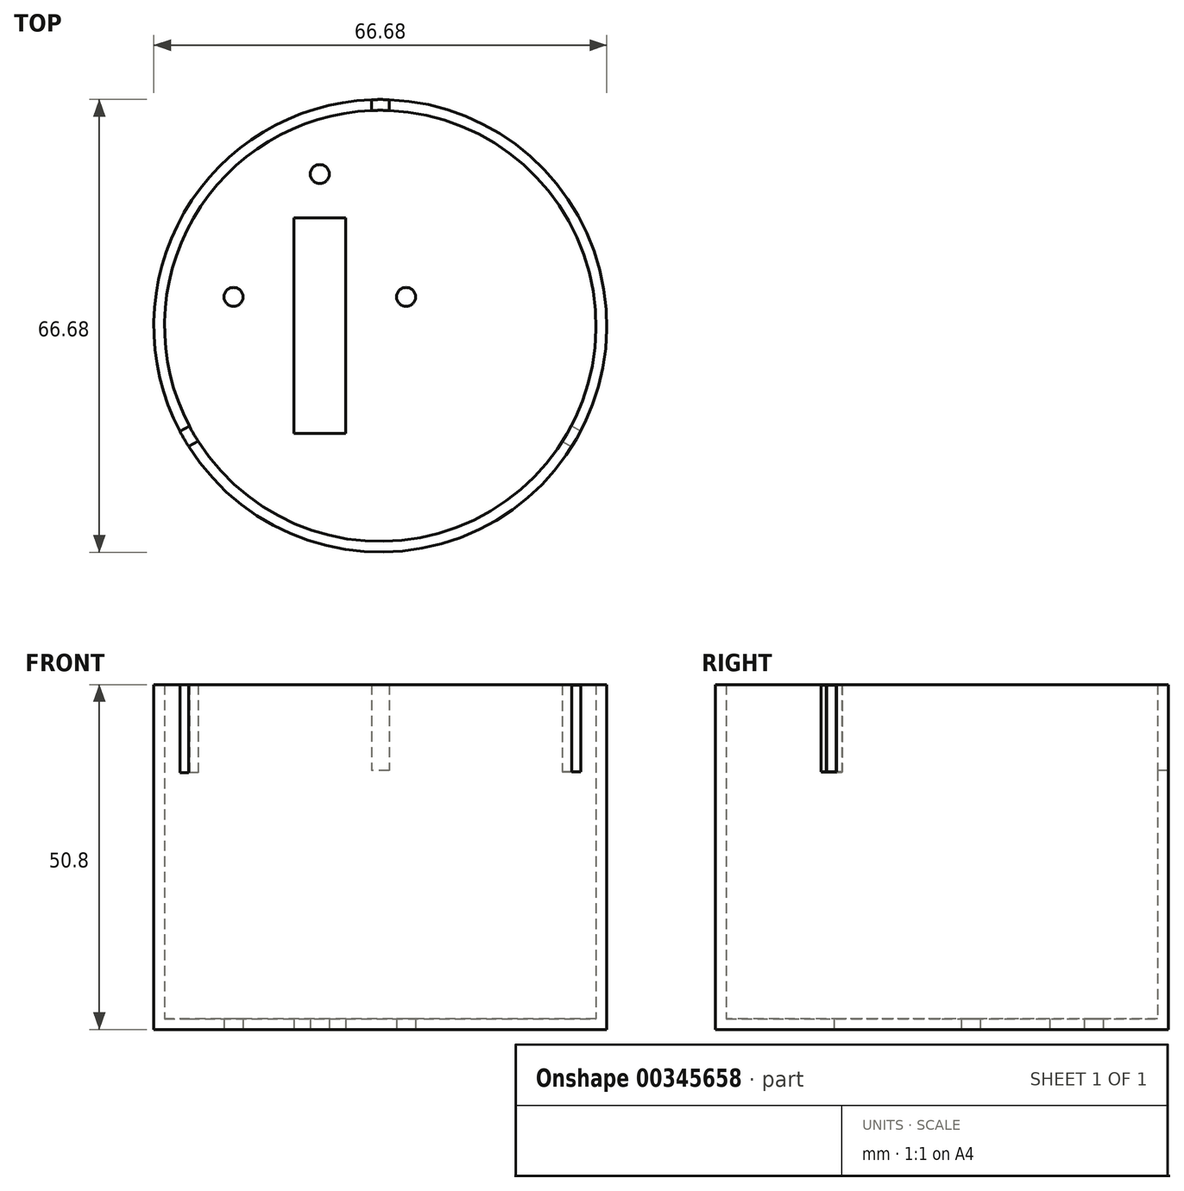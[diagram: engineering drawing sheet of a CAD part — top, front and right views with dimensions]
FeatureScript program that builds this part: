
annotation { "Feature Type Name" : "Feature", "Feature Type Description" : "" }
export const myFeature = defineFeature(function(context is Context, id is Id, definition is map)
    precondition{}
    {
        {
            var Q0;
            Q0=qCreatedBy(makeId("Top.planeOp"),FACE);
            var sketch = newSketch(context, id + "F0", { "sketchPlane" : qUnion([Q0])});
            skCircle(sketch, "E0", {"center": v(0, 0) * mm, "radius": 33.34 * mm});
            skSolve(sketch);
        }
        {
            var Q0;
            Q0=makeQuery(id+"F0.imprint","IMPRINT",FACE,{"disambiguationData":[TD([[makeQuery(id+"F0.imprint","IMPRINT",EDGE,{"derivedFrom":sQuery(id+"F0.wireOp",EDGE,"E0")}),1.0]])]});
            extrude(context, id + "F1", {"entities" : qUnion([Q0]), "depth" : 50.8 * mm});
        }
        {
            var Q0;
            Q0=makeQuery(id+"F1.opExtrude","CAP_FACE",FACE,{"disambiguationData":[OSD([sQuery(id+"F0.wireOp",EDGE,"E0")])],"isStart":false});
            shell(context, id + "F2", {"entities" : qUnion([Q0]), "thickness" : 1.59 * mm});
        }
        {
            var Q0;
            Q0=qCreatedBy(makeId("Top.planeOp"),FACE);
            var sketch = newSketch(context, id + "F3", { "sketchPlane" : qUnion([Q0])});
            skLineSegment(sketch, "E1", {"start": v(58.26, 0) * mm, "end": v(0, 0) * mm, "construction": true});
            skLineSegment(sketch, "E2", {"start": v(0, 0) * mm, "end": v(47.3, -27.3) * mm, "construction": true});
            skLineSegment(sketch, "E3", {"start": v(-50.45, 0) * mm, "end": v(0, 0) * mm, "construction": true});
            skLineSegment(sketch, "E4", {"start": v(0, 0) * mm, "end": v(-51.5, -29.73) * mm, "construction": true});
            skSolve(sketch);
        }
        {
            var Q0;
            Q0=sQuery(id+"F3.wireOp",EDGE,"E4");
            var Q1;
            Q1=sQuery(id+"F3.wireOp",VERTEX,"E4.start");
            cPlane(context, id + "F4", {"entities" : qUnion([Q0, Q1]), "cplaneType" : CPlaneType.LINE_POINT, "offset" : 25.4 * mm, "width" : 152.4 * mm, "height" : 152.4 * mm});
        }
        {
            var Q0;
            Q0=qCreatedBy(id+"F4.planeOp",FACE);
            cPlane(context, id + "F5", {"entities" : qUnion([Q0]), "cplaneType" : CPlaneType.OFFSET, "offset" : 33.34 * mm, "width" : 152.4 * mm, "height" : 152.4 * mm});
        }
        {
            var Q0;
            Q0=qCreatedBy(id+"F5.planeOp",FACE);
            var sketch = newSketch(context, id + "F6", { "sketchPlane" : qUnion([Q0])});
            skLineSegment(sketch, "E5.bottom", {"start": v(-1.27, 37.8) * mm, "end": v(1.27, 37.8) * mm});
            skLineSegment(sketch, "E5.top", {"start": v(-1.27, 51) * mm, "end": v(1.27, 51) * mm});
            skLineSegment(sketch, "E5.left", {"start": v(-1.27, 37.8) * mm, "end": v(-1.27, 51) * mm});
            skLineSegment(sketch, "E5.right", {"start": v(1.27, 37.8) * mm, "end": v(1.27, 51) * mm});
            skPoint(sketch, "E5.middle", {"position": v(0, 44.4) * mm});
            skSolve(sketch);
        }
        {
            var Q0;
            Q0=makeQuery(id+"F6.imprint","IMPRINT",FACE,{"disambiguationData":[TD([[makeQuery(id+"F6.imprint","IMPRINT",EDGE,{"derivedFrom":sQuery(id+"F6.wireOp",EDGE,"E5.bottom")}),1.0]])]});
            extrude(context, id + "F7", {"entities" : qUnion([Q0]), "operationType" : NewBodyOperationType.REMOVE, "oppositeDirection" : true, "depth" : 12.7 * mm});
        }
        {
            var Q0;
            Q0=sQuery(id+"F3.wireOp",EDGE,"E2");
            var Q1;
            Q1=sQuery(id+"F3.wireOp",VERTEX,"E4.start");
            cPlane(context, id + "F8", {"entities" : qUnion([Q0, Q1]), "cplaneType" : CPlaneType.LINE_POINT, "offset" : 25.4 * mm, "width" : 152.4 * mm, "height" : 152.4 * mm});
        }
        {
            var Q0;
            Q0=qCreatedBy(id+"F8.planeOp",FACE);
            cPlane(context, id + "F9", {"entities" : qUnion([Q0]), "cplaneType" : CPlaneType.OFFSET, "offset" : 33.27 * mm, "width" : 152.4 * mm, "height" : 152.4 * mm});
        }
        {
            var Q0;
            Q0=qCreatedBy(id+"F9.planeOp",FACE);
            var sketch = newSketch(context, id + "F10", { "sketchPlane" : qUnion([Q0])});
            skLineSegment(sketch, "E6.bottom", {"start": v(-1.34, 37.95) * mm, "end": v(1.34, 37.95) * mm});
            skLineSegment(sketch, "E6.top", {"start": v(-1.34, 50.73) * mm, "end": v(1.34, 50.73) * mm});
            skLineSegment(sketch, "E6.left", {"start": v(-1.34, 37.95) * mm, "end": v(-1.34, 50.73) * mm});
            skLineSegment(sketch, "E6.right", {"start": v(1.34, 37.95) * mm, "end": v(1.34, 50.73) * mm});
            skPoint(sketch, "E6.middle", {"position": v(0, 44.34) * mm});
            skSolve(sketch);
        }
        {
            var Q0;
            Q0=makeQuery(id+"F10.imprint","IMPRINT",FACE,{"disambiguationData":[TD([[makeQuery(id+"F10.imprint","IMPRINT",EDGE,{"derivedFrom":sQuery(id+"F10.wireOp",EDGE,"E6.bottom")}),1.0]])]});
            extrude(context, id + "F11", {"entities" : qUnion([Q0]), "operationType" : NewBodyOperationType.REMOVE, "oppositeDirection" : true, "depth" : 2.8 * mm, "hasSecondDirection" : true, "secondDirectionOppositeDirection" : false, "secondDirectionDepth" : 2.41 * mm});
        }
        {
            var Q0;
            Q0=qCreatedBy(makeId("Front.planeOp"),FACE);
            cPlane(context, id + "F12", {"entities" : qUnion([Q0]), "cplaneType" : CPlaneType.OFFSET, "offset" : 33.81 * mm, "oppositeDirection" : true, "width" : 152.4 * mm, "height" : 152.4 * mm});
        }
        {
            var Q0;
            Q0=qCreatedBy(id+"F12.planeOp",FACE);
            var sketch = newSketch(context, id + "F13", { "sketchPlane" : qUnion([Q0])});
            skLineSegment(sketch, "E7.bottom", {"start": v(1.3, 38.14) * mm, "end": v(-1.3, 38.14) * mm});
            skLineSegment(sketch, "E7.top", {"start": v(1.3, 50.9) * mm, "end": v(-1.3, 50.9) * mm});
            skLineSegment(sketch, "E7.left", {"start": v(1.3, 38.14) * mm, "end": v(1.3, 50.9) * mm});
            skLineSegment(sketch, "E7.right", {"start": v(-1.3, 38.14) * mm, "end": v(-1.3, 50.9) * mm});
            skPoint(sketch, "E7.middle", {"position": v(0, 44.52) * mm});
            skSolve(sketch);
        }
        {
            var Q0;
            Q0=makeQuery(id+"F13.imprint","IMPRINT",FACE,{"disambiguationData":[TD([[makeQuery(id+"F13.imprint","IMPRINT",EDGE,{"derivedFrom":sQuery(id+"F13.wireOp",EDGE,"E7.bottom")}),-1.0]])]});
            extrude(context, id + "F14", {"entities" : qUnion([Q0]), "operationType" : NewBodyOperationType.REMOVE, "oppositeDirection" : true, "depth" : 5.05 * mm, "hasSecondDirection" : true, "secondDirectionOppositeDirection" : false, "secondDirectionDepth" : 4.72 * mm});
        }
        {
            var Q0;
            Q0=qCreatedBy(makeId("Top.planeOp"),FACE);
            var sketch = newSketch(context, id + "F15", { "sketchPlane" : qUnion([Q0])});
            skLineSegment(sketch, "E8.bottom", {"start": v(-12.7, -15.88) * mm, "end": v(-5.08, -15.88) * mm});
            skLineSegment(sketch, "E8.top", {"start": v(-12.7, 15.88) * mm, "end": v(-5.08, 15.88) * mm});
            skLineSegment(sketch, "E8.left", {"start": v(-12.7, -15.88) * mm, "end": v(-12.7, 15.88) * mm});
            skLineSegment(sketch, "E8.right", {"start": v(-5.08, -15.88) * mm, "end": v(-5.08, 15.88) * mm});
            skLineSegment(sketch, "E9", {"start": v(0, -15.24) * mm, "end": v(20.32, -15.24) * mm, "construction": true});
            skLineSegment(sketch, "E10.right", {"start": v(-6.15, 11.35) * mm, "end": v(-6.15, 11.18) * mm});
            skLineSegment(sketch, "E11", {"start": v(-1.58, -15.49) * mm, "end": v(18.74, -15.49) * mm, "construction": true});
            skPoint(sketch, "E12.centerSnap0", {"position": v(-31.36, 0) * mm});
            skPoint(sketch, "E13.centerSnap1", {"position": v(-18.66, 21.27) * mm});
            skLineSegment(sketch, "E14", {"start": v(-8.9, -15.88) * mm, "end": v(-8.9, 35.48) * mm, "construction": true});
            skPoint(sketch, "E15.center.orphan", {"position": v(6.98, 0) * mm});
            skPoint(sketch, "E12.center.orphan", {"position": v(-24.77, 0) * mm});
            skCircle(sketch, "E16", {"center": v(-21.6, 4.25) * mm, "radius": 1.4 * mm});
            skCircle(sketch, "E17", {"center": v(3.8, 4.25) * mm, "radius": 1.4 * mm});
            skCircle(sketch, "E18", {"center": v(-8.9, 22.35) * mm, "radius": 1.4 * mm});
            skSolve(sketch);
        }
        {
            var Q0;
            Q0=makeQuery(id+"F15.imprint","IMPRINT",FACE,{"disambiguationData":[TD([[makeQuery(id+"F15.imprint","IMPRINT",EDGE,{"derivedFrom":sQuery(id+"F15.wireOp",EDGE,"E8.bottom")}),1.0]])]});
            var Q1;
            Q1=makeQuery(id+"F15.imprint","IMPRINT",FACE,{"disambiguationData":[TD([[makeQuery(id+"F15.imprint","IMPRINT",EDGE,{"derivedFrom":sQuery(id+"F15.wireOp",EDGE,"9446cff0-4111-4a2f-865f-400fcaa16339.bottom")}),1.0]])]});
            var Q2;
            Q2=makeQuery(id+"F15.imprint","IMPRINT",FACE,{"disambiguationData":[TD([[makeQuery(id+"F15.imprint","IMPRINT",EDGE,{"derivedFrom":sQuery(id+"F15.wireOp",EDGE,"9382fee4-65a7-4800-b25e-e2ef16b69689.bottom")}),1.0]])]});
            var Q3;
            Q3=makeQuery(id+"F15.imprint","IMPRINT",FACE,{"disambiguationData":[TD([[makeQuery(id+"F15.imprint","IMPRINT",EDGE,{"derivedFrom":sQuery(id+"F15.wireOp",EDGE,"46ee8cd2-13bb-4cbc-9d3f-eb22f2e6db9a.bottom")}),-1.0]])]});
            var Q4;
            Q4=makeQuery(id+"F15.imprint","IMPRINT",FACE,{"disambiguationData":[TD([[makeQuery(id+"F15.imprint","IMPRINT",EDGE,{"derivedFrom":sQuery(id+"F15.wireOp",EDGE,"E15")}),1.0]])]});
            var Q5;
            Q5=makeQuery(id+"F15.imprint","IMPRINT",FACE,{"disambiguationData":[TD([[makeQuery(id+"F15.imprint","IMPRINT",EDGE,{"derivedFrom":sQuery(id+"F15.wireOp",EDGE,"E13")}),1.0]])]});
            var Q6;
            Q6=makeQuery(id+"F15.imprint","IMPRINT",FACE,{"disambiguationData":[TD([[makeQuery(id+"F15.imprint","IMPRINT",EDGE,{"derivedFrom":sQuery(id+"F15.wireOp",EDGE,"E12")}),1.0]])]});
            var Q7;
            Q7=makeQuery(id+"F15.imprint","IMPRINT",FACE,{"disambiguationData":[TD([[makeQuery(id+"F15.imprint","IMPRINT",EDGE,{"derivedFrom":sQuery(id+"F15.wireOp",EDGE,"E16")}),1.0]])]});
            var Q8;
            Q8=makeQuery(id+"F15.imprint","IMPRINT",FACE,{"disambiguationData":[TD([[makeQuery(id+"F15.imprint","IMPRINT",EDGE,{"derivedFrom":sQuery(id+"F15.wireOp",EDGE,"E17")}),1.0]])]});
            var Q9;
            Q9=makeQuery(id+"F15.imprint","IMPRINT",FACE,{"disambiguationData":[TD([[makeQuery(id+"F15.imprint","IMPRINT",EDGE,{"derivedFrom":sQuery(id+"F15.wireOp",EDGE,"E18")}),1.0]])]});
            extrude(context, id + "F16", {"entities" : qUnion([Q0, Q1, Q2, Q3, Q4, Q5, Q6, Q7, Q8, Q9]), "operationType" : NewBodyOperationType.REMOVE, "depth" : 9.9 * mm});
        }
    });
